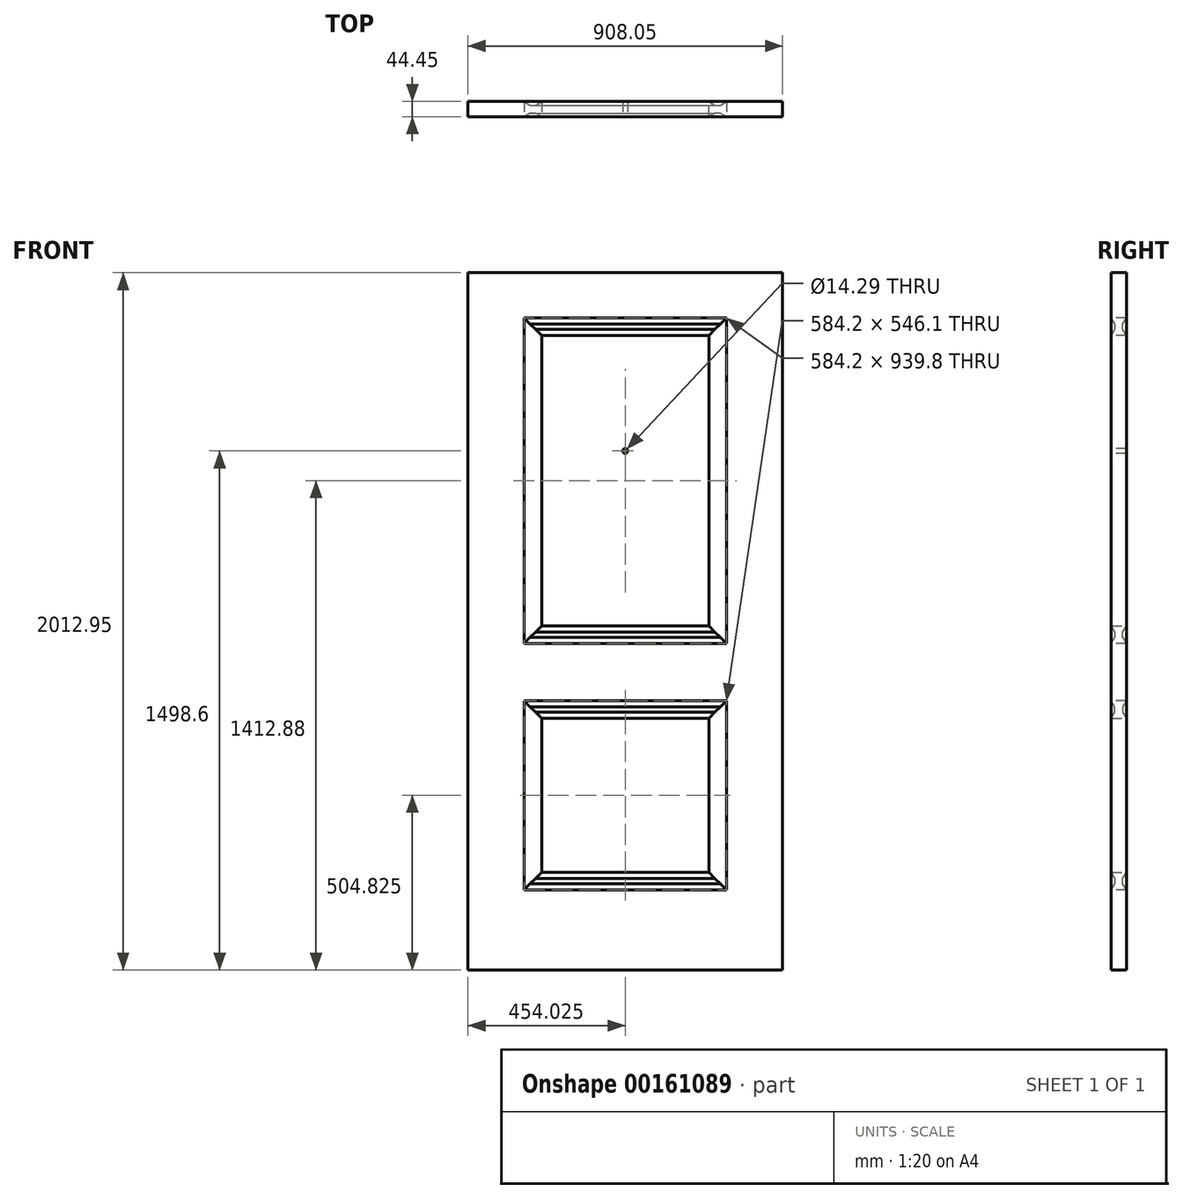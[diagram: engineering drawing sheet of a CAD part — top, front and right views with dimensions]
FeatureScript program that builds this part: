
annotation { "Feature Type Name" : "Feature", "Feature Type Description" : "" }
export const myFeature = defineFeature(function(context is Context, id is Id, definition is map)
    precondition{}
    {
        {
            var Q0;
            Q0=qCreatedBy(makeId("Top.planeOp"),FACE);
            var sketch = newSketch(context, id + "F0", { "sketchPlane" : qUnion([Q0])});
            skLineSegment(sketch, "E0.bottom", {"start": v(0, 0) * mm, "end": v(-908.05, 0) * mm});
            skLineSegment(sketch, "E0.top", {"start": v(0, 44.45) * mm, "end": v(-908.05, 44.45) * mm});
            skLineSegment(sketch, "E0.left", {"start": v(0, 0) * mm, "end": v(0, 44.45) * mm});
            skLineSegment(sketch, "E0.right", {"start": v(-908.05, 0) * mm, "end": v(-908.05, 44.45) * mm});
            skSolve(sketch);
        }
        {
            var Q0;
            Q0=qSketchRegion(id+"F0",true);
            extrude(context, id + "F1", {"entities" : qUnion([Q0]), "depth" : 2012.95 * mm});
        }
        {
            var Q0;
            Q0=qCreatedBy(makeId("Front.planeOp"),FACE);
            var sketch = newSketch(context, id + "F2", { "sketchPlane" : qUnion([Q0])});
            skLineSegment(sketch, "E1.top", {"start": v(-746.12, 942.97) * mm, "end": v(-161.92, 942.98) * mm});
            skLineSegment(sketch, "E1.left", {"start": v(-746.12, 1882.78) * mm, "end": v(-746.12, 942.97) * mm});
            skLineSegment(sketch, "E1.right", {"start": v(-161.93, 1882.78) * mm, "end": v(-161.92, 942.98) * mm});
            skLineSegment(sketch, "E2", {"start": v(-746.12, 1882.78) * mm, "end": v(-454.03, 1882.78) * mm});
            skLineSegment(sketch, "E3", {"start": v(-454.03, 1882.78) * mm, "end": v(-161.93, 1882.78) * mm});
            skPoint(sketch, "E4.0", {"position": v(-454.03, 2012.95) * mm});
            skLineSegment(sketch, "E5.bottom", {"start": v(-746.12, 777.88) * mm, "end": v(-161.92, 777.88) * mm});
            skLineSegment(sketch, "E5.top", {"start": v(-746.12, 231.78) * mm, "end": v(-161.92, 231.78) * mm});
            skLineSegment(sketch, "E5.left", {"start": v(-746.12, 777.88) * mm, "end": v(-746.12, 231.78) * mm});
            skLineSegment(sketch, "E5.right", {"start": v(-161.92, 777.88) * mm, "end": v(-161.92, 231.78) * mm});
            skSolve(sketch);
        }
        {
            var Q0;
            Q0=qSketchRegion(id+"F2",true);
            extrude(context, id + "F3", {"entities" : qUnion([Q0]), "operationType" : NewBodyOperationType.REMOVE, "endBound" : BoundingType.THROUGH_ALL, "oppositeDirection" : true, "depth" : 25.4 * mm});
        }
        {
            var Q0;
            Q0=qCreatedBy(makeId("Top.planeOp"),FACE);
            var sketch = newSketch(context, id + "F4", { "sketchPlane" : qUnion([Q0])});
            skPoint(sketch, "E6.0", {"position": v(-161.93, 22.23) * mm});
            skPoint(sketch, "E7.0", {"position": v(-161.93, 44.45) * mm});
            skLineSegment(sketch, "E8", {"start": v(-161.93, 22.23) * mm, "end": v(-161.93, 44.45) * mm});
            skLineSegment(sketch, "E9", {"start": v(-161.93, 44.45) * mm, "end": v(-179.4, 33.62) * mm});
            skLineSegment(sketch, "E10", {"start": v(-179.4, 33.62) * mm, "end": v(-187.33, 33.62) * mm});
            skLineSegment(sketch, "E11", {"start": v(-187.33, 33.62) * mm, "end": v(-187.33, 59.2) * mm, "construction": true});
            skLineSegment(sketch, "E12", {"start": v(-161.93, 22.23) * mm, "end": v(-138.76, 22.23) * mm, "construction": true});
            skLineSegment(sketch, "E13.MirrorCS", {"start": v(-195.26, 33.62) * mm, "end": v(-187.33, 33.62) * mm});
            skLineSegment(sketch, "E14.MirrorCS", {"start": v(-212.73, 44.45) * mm, "end": v(-195.26, 33.62) * mm});
            skLineSegment(sketch, "E15.MirrorCS", {"start": v(-212.73, 22.23) * mm, "end": v(-212.73, 44.45) * mm});
            skLineSegment(sketch, "E16.MirrorCS", {"start": v(-161.93, 22.23) * mm, "end": v(-161.93, 0) * mm});
            skLineSegment(sketch, "E17.MirrorCS", {"start": v(-161.93, 0) * mm, "end": v(-179.4, 10.83) * mm});
            skLineSegment(sketch, "E18.MirrorCS", {"start": v(-179.4, 10.83) * mm, "end": v(-187.33, 10.83) * mm});
            skLineSegment(sketch, "E19.MirrorCS", {"start": v(-195.26, 10.83) * mm, "end": v(-187.33, 10.83) * mm});
            skLineSegment(sketch, "E20.MirrorCS", {"start": v(-212.73, 0) * mm, "end": v(-195.26, 10.83) * mm});
            skLineSegment(sketch, "E21.MirrorCS", {"start": v(-212.73, 22.23) * mm, "end": v(-212.73, 0) * mm});
            skPoint(sketch, "E22.0", {"position": v(-746.12, 22.23) * mm});
            skLineSegment(sketch, "E23", {"start": v(-746.12, 130.05) * mm, "end": v(-161.92, 130.05) * mm, "construction": true});
            skLineSegment(sketch, "E24", {"start": v(-454.03, 130.05) * mm, "end": v(-454.03, 201.62) * mm, "construction": true});
            skLineSegment(sketch, "E25.MirrorCS", {"start": v(-712.8, 33.62) * mm, "end": v(-720.72, 33.62) * mm});
            skPoint(sketch, "E26.MirrorP", {"position": v(-746.12, 44.45) * mm});
            skLineSegment(sketch, "E27.MirrorCS", {"start": v(-746.12, 0) * mm, "end": v(-728.66, 10.83) * mm});
            skLineSegment(sketch, "E28.MirrorCS", {"start": v(-695.32, 0) * mm, "end": v(-712.8, 10.83) * mm});
            skLineSegment(sketch, "E29.MirrorCS", {"start": v(-746.12, 22.23) * mm, "end": v(-746.12, 0) * mm});
            skLineSegment(sketch, "E30.MirrorCS", {"start": v(-695.32, 22.23) * mm, "end": v(-695.32, 0) * mm});
            skLineSegment(sketch, "E31.MirrorCS", {"start": v(-746.12, 44.45) * mm, "end": v(-728.66, 33.62) * mm});
            skLineSegment(sketch, "E32.MirrorCS", {"start": v(-695.32, 44.45) * mm, "end": v(-712.8, 33.62) * mm});
            skLineSegment(sketch, "E33.MirrorCS", {"start": v(-746.12, 22.23) * mm, "end": v(-746.12, 44.45) * mm});
            skLineSegment(sketch, "E34.MirrorCS", {"start": v(-728.66, 33.62) * mm, "end": v(-720.72, 33.62) * mm});
            skLineSegment(sketch, "E35.MirrorCS", {"start": v(-712.8, 10.83) * mm, "end": v(-720.72, 10.83) * mm});
            skLineSegment(sketch, "E36.MirrorCS", {"start": v(-695.32, 22.23) * mm, "end": v(-695.32, 44.45) * mm});
            skLineSegment(sketch, "E37.MirrorCS", {"start": v(-728.66, 10.83) * mm, "end": v(-720.72, 10.83) * mm});
            skSolve(sketch);
        }
        {
            var Q0;
            Q0=qCreatedBy(makeId("Front.planeOp"),FACE);
            var sketch = newSketch(context, id + "F5", { "sketchPlane" : qUnion([Q0])});
            skPoint(sketch, "E38.0", {"position": v(-746.12, 1882.78) * mm});
            skPoint(sketch, "E39.0", {"position": v(-161.93, 1882.78) * mm});
            skPoint(sketch, "E40.0", {"position": v(-161.92, 942.97) * mm});
            skPoint(sketch, "E41.0", {"position": v(-746.12, 942.97) * mm});
            skPoint(sketch, "E42.0", {"position": v(-746.12, 777.88) * mm});
            skPoint(sketch, "E43.0", {"position": v(-161.92, 777.88) * mm});
            skPoint(sketch, "E44.0", {"position": v(-746.12, 231.78) * mm});
            skPoint(sketch, "E45.0", {"position": v(-161.92, 231.78) * mm});
            skLineSegment(sketch, "E46", {"start": v(-746.12, 1882.78) * mm, "end": v(-454.02, 1590.68) * mm});
            skLineSegment(sketch, "E47", {"start": v(-454.02, 1590.68) * mm, "end": v(-161.92, 1882.78) * mm});
            skLineSegment(sketch, "E48", {"start": v(-746.12, 777.88) * mm, "end": v(-454.02, 485.78) * mm});
            skLineSegment(sketch, "E49", {"start": v(-454.02, 485.78) * mm, "end": v(-161.93, 777.88) * mm});
            skLineSegment(sketch, "E50", {"start": v(-746.12, 1882.78) * mm, "end": v(-876.3, 2012.95) * mm});
            skLineSegment(sketch, "E51", {"start": v(-876.3, 2012.95) * mm, "end": v(-31.75, 2012.95) * mm});
            skLineSegment(sketch, "E52", {"start": v(-31.75, 2012.95) * mm, "end": v(-161.93, 1882.78) * mm});
            skLineSegment(sketch, "E53", {"start": v(-746.12, 777.88) * mm, "end": v(-1981.2, 2012.95) * mm});
            skLineSegment(sketch, "E54", {"start": v(-1981.2, 2012.95) * mm, "end": v(1073.15, 2012.95) * mm});
            skLineSegment(sketch, "E55", {"start": v(1073.15, 2012.95) * mm, "end": v(-161.93, 777.88) * mm});
            skLineSegment(sketch, "E56", {"start": v(-746.12, 942.97) * mm, "end": v(-454.03, 1235.07) * mm});
            skLineSegment(sketch, "E57", {"start": v(-454.02, 1235.08) * mm, "end": v(-161.92, 942.98) * mm});
            skLineSegment(sketch, "E58", {"start": v(-746.12, 231.77) * mm, "end": v(-454.02, 523.88) * mm});
            skLineSegment(sketch, "E59", {"start": v(-454.02, 523.88) * mm, "end": v(-161.92, 231.78) * mm});
            skLineSegment(sketch, "E60", {"start": v(-746.13, 942.97) * mm, "end": v(-1689.1, 0) * mm});
            skLineSegment(sketch, "E61", {"start": v(-1689.1, 0) * mm, "end": v(781.05, 0) * mm});
            skLineSegment(sketch, "E62", {"start": v(781.05, 0) * mm, "end": v(-161.92, 942.97) * mm});
            skLineSegment(sketch, "E63", {"start": v(-161.92, 231.78) * mm, "end": v(69.85, 0) * mm});
            skLineSegment(sketch, "E64", {"start": v(69.85, 0) * mm, "end": v(-977.9, 0) * mm});
            skLineSegment(sketch, "E65", {"start": v(-977.9, 0) * mm, "end": v(-746.12, 231.78) * mm});
            skSolve(sketch);
        }
        {
            var Q0;
            Q0=makeQuery(id+"F3.boolean.opBoolean","COPY",FACE,{"derivedFrom":makeQuery(id+"F3.opExtrude","SWEPT_FACE",FACE,{"disambiguationData":[OSD([sQuery(id+"F2.wireOp",EDGE,"E2"),sQuery(id+"F2.wireOp",EDGE,"E3")])]})});
            var sketch = newSketch(context, id + "F6", { "sketchPlane" : qUnion([Q0])});
            skLineSegment(sketch, "E66.4", {"start": v(-212.73, -44.45) * mm, "end": v(-195.26, -33.62) * mm});
            skLineSegment(sketch, "E66.6", {"start": v(-212.73, -22.23) * mm, "end": v(-212.73, -44.45) * mm});
            skLineSegment(sketch, "E66.8", {"start": v(-212.73, 0) * mm, "end": v(-195.26, -10.83) * mm});
            skLineSegment(sketch, "E66.9", {"start": v(-212.73, -22.23) * mm, "end": v(-212.73, 0) * mm});
            skLineSegment(sketch, "E66.11", {"start": v(-161.93, -44.45) * mm, "end": v(-179.4, -33.62) * mm});
            skLineSegment(sketch, "E66.14", {"start": v(-195.26, -33.62) * mm, "end": v(-187.33, -33.62) * mm});
            skLineSegment(sketch, "E66.16", {"start": v(-161.93, -22.23) * mm, "end": v(-161.93, 0) * mm});
            skLineSegment(sketch, "E66.17", {"start": v(-161.93, 0) * mm, "end": v(-179.4, -10.83) * mm});
            skLineSegment(sketch, "E66.18", {"start": v(-179.4, -10.83) * mm, "end": v(-187.33, -10.83) * mm});
            skLineSegment(sketch, "E66.19", {"start": v(-195.26, -10.83) * mm, "end": v(-187.33, -10.83) * mm});
            skLineSegment(sketch, "E66.25", {"start": v(-161.93, -22.23) * mm, "end": v(-161.93, -44.45) * mm});
            skLineSegment(sketch, "E66.26", {"start": v(-179.4, -33.62) * mm, "end": v(-187.33, -33.62) * mm});
            skLineSegment(sketch, "E67.0", {"start": v(-746.12, -22.23) * mm, "end": v(-746.12, 0) * mm});
            skLineSegment(sketch, "E68.0", {"start": v(-746.12, 0) * mm, "end": v(-728.66, -10.83) * mm});
            skLineSegment(sketch, "E69.0", {"start": v(-728.66, -10.83) * mm, "end": v(-720.72, -10.83) * mm});
            skLineSegment(sketch, "E70.0", {"start": v(-712.8, -10.83) * mm, "end": v(-720.72, -10.83) * mm});
            skLineSegment(sketch, "E71.0", {"start": v(-695.32, 0) * mm, "end": v(-712.8, -10.83) * mm});
            skLineSegment(sketch, "E72.0", {"start": v(-695.32, -22.23) * mm, "end": v(-695.32, 0) * mm});
            skLineSegment(sketch, "E73.0", {"start": v(-695.32, -22.23) * mm, "end": v(-695.32, -44.45) * mm});
            skLineSegment(sketch, "E74.0", {"start": v(-695.32, -44.45) * mm, "end": v(-712.8, -33.62) * mm});
            skLineSegment(sketch, "E75.0", {"start": v(-712.8, -33.62) * mm, "end": v(-720.72, -33.62) * mm});
            skLineSegment(sketch, "E76.0", {"start": v(-728.66, -33.62) * mm, "end": v(-720.72, -33.62) * mm});
            skLineSegment(sketch, "E77.0", {"start": v(-746.12, -44.45) * mm, "end": v(-728.66, -33.62) * mm});
            skLineSegment(sketch, "E78.0", {"start": v(-746.12, -22.23) * mm, "end": v(-746.12, -44.45) * mm});
            skSolve(sketch);
        }
        {
            var Q0;
            Q0=makeQuery(id+"F3.boolean.opBoolean","COPY",FACE,{"derivedFrom":makeQuery(id+"F3.opExtrude","SWEPT_FACE",FACE,{"disambiguationData":[OSD([sQuery(id+"F2.wireOp",EDGE,"E5.top")])]})});
            var sketch = newSketch(context, id + "F7", { "sketchPlane" : qUnion([Q0])});
            skLineSegment(sketch, "E79.0", {"start": v(-212.73, 22.23) * mm, "end": v(-212.73, 0) * mm});
            skLineSegment(sketch, "E79.1", {"start": v(-161.93, 22.23) * mm, "end": v(-161.93, 44.45) * mm});
            skLineSegment(sketch, "E79.2", {"start": v(-161.93, 44.45) * mm, "end": v(-179.4, 33.62) * mm});
            skLineSegment(sketch, "E79.3", {"start": v(-179.4, 33.62) * mm, "end": v(-187.33, 33.62) * mm});
            skLineSegment(sketch, "E79.4", {"start": v(-195.26, 33.62) * mm, "end": v(-187.33, 33.62) * mm});
            skLineSegment(sketch, "E79.5", {"start": v(-212.73, 44.45) * mm, "end": v(-195.26, 33.62) * mm});
            skLineSegment(sketch, "E79.6", {"start": v(-212.73, 22.23) * mm, "end": v(-212.73, 44.45) * mm});
            skLineSegment(sketch, "E79.7", {"start": v(-161.93, 22.23) * mm, "end": v(-161.93, 0) * mm});
            skLineSegment(sketch, "E79.8", {"start": v(-161.93, 0) * mm, "end": v(-179.4, 10.83) * mm});
            skLineSegment(sketch, "E79.9", {"start": v(-179.4, 10.83) * mm, "end": v(-187.33, 10.83) * mm});
            skLineSegment(sketch, "E79.10", {"start": v(-195.26, 10.83) * mm, "end": v(-187.33, 10.83) * mm});
            skLineSegment(sketch, "E79.11", {"start": v(-212.73, 0) * mm, "end": v(-195.26, 10.83) * mm});
            skLineSegment(sketch, "E80.0", {"start": v(-746.12, 44.45) * mm, "end": v(-728.66, 33.62) * mm});
            skLineSegment(sketch, "E81.0", {"start": v(-746.12, 22.23) * mm, "end": v(-746.12, 44.45) * mm});
            skLineSegment(sketch, "E82.0", {"start": v(-746.12, 22.23) * mm, "end": v(-746.12, 0) * mm});
            skLineSegment(sketch, "E83.0", {"start": v(-746.12, 0) * mm, "end": v(-728.66, 10.83) * mm});
            skLineSegment(sketch, "E84.0", {"start": v(-728.66, 10.83) * mm, "end": v(-720.72, 10.83) * mm});
            skLineSegment(sketch, "E85.0", {"start": v(-712.8, 10.83) * mm, "end": v(-720.72, 10.83) * mm});
            skLineSegment(sketch, "E86.0", {"start": v(-695.32, 0) * mm, "end": v(-712.8, 10.83) * mm});
            skLineSegment(sketch, "E87.0", {"start": v(-695.32, 22.23) * mm, "end": v(-695.32, 0) * mm});
            skLineSegment(sketch, "E88.0", {"start": v(-695.32, 22.23) * mm, "end": v(-695.32, 44.45) * mm});
            skLineSegment(sketch, "E89.0", {"start": v(-695.32, 44.45) * mm, "end": v(-712.8, 33.62) * mm});
            skLineSegment(sketch, "E90.0", {"start": v(-712.8, 33.62) * mm, "end": v(-720.72, 33.62) * mm});
            skPoint(sketch, "E91.0", {"position": v(-724.7, 33.62) * mm});
            skLineSegment(sketch, "E92.0", {"start": v(-728.66, 33.62) * mm, "end": v(-720.72, 33.62) * mm});
            skSolve(sketch);
        }
        {
            var Q0;
            Q0=qSketchRegion(id+"F6",true);
            var Q1;
            Q1=makeQuery(id+"F3.boolean.opBoolean","COPY",FACE,{"derivedFrom":makeQuery(id+"F3.opExtrude","SWEPT_FACE",FACE,{"disambiguationData":[OSD([sQuery(id+"F2.wireOp",EDGE,"E1.top")])]})});
            extrude(context, id + "F8", {"entities" : qUnion([Q0]), "operationType" : NewBodyOperationType.ADD, "endBound" : BoundingType.UP_TO_SURFACE, "endBoundEntityFace" : qUnion([Q1]), "depth" : 307.34 * mm});
        }
        {
            var Q0;
            Q0=qSketchRegion(id+"F7",true);
            var Q1;
            Q1=makeQuery(id+"F3.boolean.opBoolean","COPY",FACE,{"derivedFrom":makeQuery(id+"F3.opExtrude","SWEPT_FACE",FACE,{"disambiguationData":[OSD([sQuery(id+"F2.wireOp",EDGE,"E5.bottom")])]})});
            extrude(context, id + "F9", {"entities" : qUnion([Q0]), "operationType" : NewBodyOperationType.ADD, "endBound" : BoundingType.UP_TO_SURFACE, "endBoundEntityFace" : qUnion([Q1]), "depth" : 25.4 * mm});
        }
        {
            var Q0;
            Q0=qCreatedBy(makeId("Front.planeOp"),FACE);
            var sketch = newSketch(context, id + "F10", { "sketchPlane" : qUnion([Q0])});
            skLineSegment(sketch, "E93.0", {"start": v(-454.02, 1590.68) * mm, "end": v(-161.92, 1882.78) * mm});
            skLineSegment(sketch, "E94.0", {"start": v(-746.12, 1882.78) * mm, "end": v(-454.02, 1590.68) * mm});
            skLineSegment(sketch, "E95.0", {"start": v(-454.02, 1235.08) * mm, "end": v(-161.92, 942.98) * mm});
            skLineSegment(sketch, "E96.0", {"start": v(-746.12, 942.97) * mm, "end": v(-454.03, 1235.07) * mm});
            skLineSegment(sketch, "E97.0", {"start": v(-454.02, 485.78) * mm, "end": v(-161.92, 777.88) * mm});
            skLineSegment(sketch, "E98.0", {"start": v(-746.12, 777.88) * mm, "end": v(-454.02, 485.78) * mm});
            skLineSegment(sketch, "E99.0", {"start": v(-746.12, 231.77) * mm, "end": v(-454.02, 523.88) * mm});
            skLineSegment(sketch, "E100.0", {"start": v(-454.02, 523.88) * mm, "end": v(-161.92, 231.78) * mm});
            skLineSegment(sketch, "E101", {"start": v(-746.12, 1882.78) * mm, "end": v(-161.92, 1882.78) * mm});
            skLineSegment(sketch, "E102", {"start": v(-746.12, 942.97) * mm, "end": v(-161.92, 942.97) * mm});
            skLineSegment(sketch, "E103", {"start": v(-161.92, 777.88) * mm, "end": v(-746.12, 777.88) * mm});
            skLineSegment(sketch, "E104", {"start": v(-746.12, 231.77) * mm, "end": v(-161.92, 231.78) * mm});
            skSolve(sketch);
        }
        {
            var Q0;
            Q0=qSketchRegion(id+"F10",true);
            extrude(context, id + "F11", {"entities" : qUnion([Q0]), "operationType" : NewBodyOperationType.REMOVE, "endBound" : BoundingType.THROUGH_ALL, "oppositeDirection" : true, "depth" : 25.4 * mm});
        }
        {
            var Q0;
            Q0=qCreatedBy(makeId("Right.planeOp"),FACE);
            var sketch = newSketch(context, id + "F12", { "sketchPlane" : qUnion([Q0])});
            skLineSegment(sketch, "E105.0.0", {"start": v(0, 1882.78) * mm, "end": v(44.45, 1882.78) * mm});
            skLineSegment(sketch, "E105.0.1", {"start": v(44.45, 1882.78) * mm, "end": v(33.62, 1865.3) * mm});
            skLineSegment(sketch, "E105.0.2", {"start": v(33.62, 1865.3) * mm, "end": v(33.62, 1849.44) * mm});
            skLineSegment(sketch, "E105.0.3", {"start": v(33.62, 1849.44) * mm, "end": v(44.45, 1831.98) * mm});
            skLineSegment(sketch, "E105.0.4", {"start": v(44.45, 1831.97) * mm, "end": v(0, 1831.97) * mm});
            skLineSegment(sketch, "E105.0.5", {"start": v(0, 1831.98) * mm, "end": v(10.83, 1849.44) * mm});
            skLineSegment(sketch, "E105.0.6", {"start": v(10.83, 1849.44) * mm, "end": v(10.83, 1865.3) * mm});
            skLineSegment(sketch, "E105.0.7", {"start": v(10.83, 1865.3) * mm, "end": v(0, 1882.77) * mm});
            skLineSegment(sketch, "E106.0.0", {"start": v(0, 942.98) * mm, "end": v(10.83, 960.44) * mm});
            skLineSegment(sketch, "E106.0.1", {"start": v(10.83, 960.44) * mm, "end": v(10.83, 976.3) * mm});
            skLineSegment(sketch, "E106.0.2", {"start": v(10.83, 976.3) * mm, "end": v(0, 993.77) * mm});
            skLineSegment(sketch, "E106.0.3", {"start": v(0, 993.77) * mm, "end": v(44.45, 993.77) * mm});
            skLineSegment(sketch, "E106.0.4", {"start": v(44.45, 993.77) * mm, "end": v(33.62, 976.3) * mm});
            skLineSegment(sketch, "E106.0.5", {"start": v(33.62, 976.3) * mm, "end": v(33.62, 960.44) * mm});
            skLineSegment(sketch, "E106.0.6", {"start": v(33.62, 960.44) * mm, "end": v(44.45, 942.97) * mm});
            skLineSegment(sketch, "E106.0.7", {"start": v(44.45, 942.98) * mm, "end": v(0, 942.98) * mm});
            skLineSegment(sketch, "E107.0.0", {"start": v(33.62, 760.4) * mm, "end": v(33.62, 744.54) * mm});
            skLineSegment(sketch, "E107.0.1", {"start": v(33.62, 744.54) * mm, "end": v(44.45, 727.07) * mm});
            skLineSegment(sketch, "E107.0.2", {"start": v(44.45, 727.07) * mm, "end": v(0, 727.07) * mm});
            skLineSegment(sketch, "E107.0.3", {"start": v(0, 727.08) * mm, "end": v(10.83, 744.54) * mm});
            skLineSegment(sketch, "E107.0.4", {"start": v(10.83, 744.54) * mm, "end": v(10.83, 760.4) * mm});
            skLineSegment(sketch, "E107.0.5", {"start": v(10.83, 760.4) * mm, "end": v(0, 777.88) * mm});
            skLineSegment(sketch, "E107.0.6", {"start": v(0, 777.88) * mm, "end": v(44.45, 777.88) * mm});
            skLineSegment(sketch, "E107.0.7", {"start": v(44.45, 777.87) * mm, "end": v(33.62, 760.4) * mm});
            skLineSegment(sketch, "E108.0.0", {"start": v(33.62, 249.24) * mm, "end": v(44.45, 231.77) * mm});
            skLineSegment(sketch, "E108.0.1", {"start": v(44.45, 231.78) * mm, "end": v(0, 231.78) * mm});
            skLineSegment(sketch, "E108.0.2", {"start": v(0, 231.78) * mm, "end": v(10.83, 249.24) * mm});
            skLineSegment(sketch, "E108.0.3", {"start": v(10.83, 249.24) * mm, "end": v(10.83, 265.1) * mm});
            skLineSegment(sketch, "E108.0.4", {"start": v(10.83, 265.1) * mm, "end": v(0, 282.58) * mm});
            skLineSegment(sketch, "E108.0.5", {"start": v(0, 282.58) * mm, "end": v(44.45, 282.58) * mm});
            skLineSegment(sketch, "E108.0.6", {"start": v(44.45, 282.57) * mm, "end": v(33.62, 265.1) * mm});
            skLineSegment(sketch, "E108.0.7", {"start": v(33.62, 265.1) * mm, "end": v(33.62, 249.24) * mm});
            skSolve(sketch);
        }
        {
            var Q0;
            Q0=qSketchRegion(id+"F12",true);
            var Q1;
            Q1=makeQuery(id+"F1.opExtrude","SWEPT_FACE",FACE,{"disambiguationData":[OSD([sQuery(id+"F0.wireOp",EDGE,"E0.right")])]});
            extrude(context, id + "F13", {"entities" : qUnion([Q0]), "endBound" : BoundingType.UP_TO_SURFACE, "oppositeDirection" : true, "endBoundEntityFace" : qUnion([Q1]), "depth" : 25.4 * mm});
        }
        {
            var Q0;
            Q0=qCreatedBy(makeId("Front.planeOp"),FACE);
            var sketch = newSketch(context, id + "F14", { "sketchPlane" : qUnion([Q0])});
            skLineSegment(sketch, "E109.0", {"start": v(-746.12, 231.77) * mm, "end": v(-454.02, 523.88) * mm});
            skLineSegment(sketch, "E110.0", {"start": v(-746.12, 777.88) * mm, "end": v(-454.02, 485.78) * mm});
            skLineSegment(sketch, "E111.0", {"start": v(-454.02, 523.88) * mm, "end": v(-161.92, 231.78) * mm});
            skLineSegment(sketch, "E112.0", {"start": v(-454.02, 485.78) * mm, "end": v(-161.92, 777.88) * mm});
            skLineSegment(sketch, "E113", {"start": v(-161.92, 777.88) * mm, "end": v(-161.92, 231.78) * mm});
            skLineSegment(sketch, "E114", {"start": v(-746.12, 777.88) * mm, "end": v(-746.12, 231.77) * mm});
            skLineSegment(sketch, "E115.0", {"start": v(-454.02, 1590.68) * mm, "end": v(-161.92, 1882.78) * mm});
            skLineSegment(sketch, "E116.0", {"start": v(-746.12, 1882.78) * mm, "end": v(-454.02, 1590.68) * mm});
            skLineSegment(sketch, "E117.0", {"start": v(-746.12, 942.97) * mm, "end": v(-454.03, 1235.07) * mm});
            skLineSegment(sketch, "E118.0", {"start": v(-454.02, 1235.08) * mm, "end": v(-161.92, 942.98) * mm});
            skLineSegment(sketch, "E119", {"start": v(-161.92, 1882.78) * mm, "end": v(-161.92, 942.98) * mm});
            skLineSegment(sketch, "E120", {"start": v(-746.12, 942.97) * mm, "end": v(-746.12, 1882.78) * mm});
            skSolve(sketch);
        }
        {
            var Q0;
            Q0=qSketchRegion(id+"F14",true);
            extrude(context, id + "F15", {"entities" : qUnion([Q0]), "operationType" : NewBodyOperationType.REMOVE, "endBound" : BoundingType.THROUGH_ALL, "oppositeDirection" : true, "depth" : 25.4 * mm});
        }
        {
            var Q0;
            Q0=makeQuery(id+"F1.opExtrude","SWEPT_BODY",BODY,{"disambiguationData":[OSD([sQuery(id+"F0.wireOp",EDGE,"E0.bottom"),sQuery(id+"F0.wireOp",EDGE,"E0.top"),sQuery(id+"F0.wireOp",EDGE,"E0.left"),sQuery(id+"F0.wireOp",EDGE,"E0.right")])]});
            var Q1;
            Q1=makeQuery(id+"F15.boolean.opBoolean","SPLIT",BODY,{"disambiguationData":[OD(0.0)],"derivedFrom":makeQuery(id+"F13.opExtrude","SWEPT_BODY",BODY,{"disambiguationData":[OSD([sQuery(id+"F12.wireOp",EDGE,"E105.0.0"),sQuery(id+"F12.wireOp",EDGE,"E105.0.1"),sQuery(id+"F12.wireOp",EDGE,"E105.0.2"),sQuery(id+"F12.wireOp",EDGE,"E105.0.3"),sQuery(id+"F12.wireOp",EDGE,"E105.0.4"),sQuery(id+"F12.wireOp",EDGE,"E105.0.5"),sQuery(id+"F12.wireOp",EDGE,"E105.0.6"),sQuery(id+"F12.wireOp",EDGE,"E105.0.7")])]})});
            var Q2;
            Q2=makeQuery(id+"F15.boolean.opBoolean","SPLIT",BODY,{"disambiguationData":[OD(1.0)],"derivedFrom":makeQuery(id+"F13.opExtrude","SWEPT_BODY",BODY,{"disambiguationData":[OSD([sQuery(id+"F12.wireOp",EDGE,"E105.0.0"),sQuery(id+"F12.wireOp",EDGE,"E105.0.1"),sQuery(id+"F12.wireOp",EDGE,"E105.0.2"),sQuery(id+"F12.wireOp",EDGE,"E105.0.3"),sQuery(id+"F12.wireOp",EDGE,"E105.0.4"),sQuery(id+"F12.wireOp",EDGE,"E105.0.5"),sQuery(id+"F12.wireOp",EDGE,"E105.0.6"),sQuery(id+"F12.wireOp",EDGE,"E105.0.7")])]})});
            var Q3;
            Q3=makeQuery(id+"F15.boolean.opBoolean","SPLIT",BODY,{"disambiguationData":[OD(2.0)],"derivedFrom":makeQuery(id+"F13.opExtrude","SWEPT_BODY",BODY,{"disambiguationData":[OSD([sQuery(id+"F12.wireOp",EDGE,"E105.0.0"),sQuery(id+"F12.wireOp",EDGE,"E105.0.1"),sQuery(id+"F12.wireOp",EDGE,"E105.0.2"),sQuery(id+"F12.wireOp",EDGE,"E105.0.3"),sQuery(id+"F12.wireOp",EDGE,"E105.0.4"),sQuery(id+"F12.wireOp",EDGE,"E105.0.5"),sQuery(id+"F12.wireOp",EDGE,"E105.0.6"),sQuery(id+"F12.wireOp",EDGE,"E105.0.7")])]})});
            var Q4;
            Q4=makeQuery(id+"F15.boolean.opBoolean","SPLIT",BODY,{"disambiguationData":[OD(0.0)],"derivedFrom":makeQuery(id+"F13.opExtrude","SWEPT_BODY",BODY,{"disambiguationData":[OSD([sQuery(id+"F12.wireOp",EDGE,"E106.0.0"),sQuery(id+"F12.wireOp",EDGE,"E106.0.1"),sQuery(id+"F12.wireOp",EDGE,"E106.0.2"),sQuery(id+"F12.wireOp",EDGE,"E106.0.3"),sQuery(id+"F12.wireOp",EDGE,"E106.0.4"),sQuery(id+"F12.wireOp",EDGE,"E106.0.5"),sQuery(id+"F12.wireOp",EDGE,"E106.0.6"),sQuery(id+"F12.wireOp",EDGE,"E106.0.7")])]})});
            var Q5;
            Q5=makeQuery(id+"F15.boolean.opBoolean","SPLIT",BODY,{"disambiguationData":[OD(1.0)],"derivedFrom":makeQuery(id+"F13.opExtrude","SWEPT_BODY",BODY,{"disambiguationData":[OSD([sQuery(id+"F12.wireOp",EDGE,"E106.0.0"),sQuery(id+"F12.wireOp",EDGE,"E106.0.1"),sQuery(id+"F12.wireOp",EDGE,"E106.0.2"),sQuery(id+"F12.wireOp",EDGE,"E106.0.3"),sQuery(id+"F12.wireOp",EDGE,"E106.0.4"),sQuery(id+"F12.wireOp",EDGE,"E106.0.5"),sQuery(id+"F12.wireOp",EDGE,"E106.0.6"),sQuery(id+"F12.wireOp",EDGE,"E106.0.7")])]})});
            var Q6;
            Q6=makeQuery(id+"F15.boolean.opBoolean","SPLIT",BODY,{"disambiguationData":[OD(2.0)],"derivedFrom":makeQuery(id+"F13.opExtrude","SWEPT_BODY",BODY,{"disambiguationData":[OSD([sQuery(id+"F12.wireOp",EDGE,"E106.0.0"),sQuery(id+"F12.wireOp",EDGE,"E106.0.1"),sQuery(id+"F12.wireOp",EDGE,"E106.0.2"),sQuery(id+"F12.wireOp",EDGE,"E106.0.3"),sQuery(id+"F12.wireOp",EDGE,"E106.0.4"),sQuery(id+"F12.wireOp",EDGE,"E106.0.5"),sQuery(id+"F12.wireOp",EDGE,"E106.0.6"),sQuery(id+"F12.wireOp",EDGE,"E106.0.7")])]})});
            var Q7;
            Q7=makeQuery(id+"F15.boolean.opBoolean","SPLIT",BODY,{"disambiguationData":[OD(0.0)],"derivedFrom":makeQuery(id+"F13.opExtrude","SWEPT_BODY",BODY,{"disambiguationData":[OSD([sQuery(id+"F12.wireOp",EDGE,"E107.0.0"),sQuery(id+"F12.wireOp",EDGE,"E107.0.1"),sQuery(id+"F12.wireOp",EDGE,"E107.0.2"),sQuery(id+"F12.wireOp",EDGE,"E107.0.3"),sQuery(id+"F12.wireOp",EDGE,"E107.0.4"),sQuery(id+"F12.wireOp",EDGE,"E107.0.5"),sQuery(id+"F12.wireOp",EDGE,"E107.0.6"),sQuery(id+"F12.wireOp",EDGE,"E107.0.7")])]})});
            var Q8;
            Q8=makeQuery(id+"F15.boolean.opBoolean","SPLIT",BODY,{"disambiguationData":[OD(1.0)],"derivedFrom":makeQuery(id+"F13.opExtrude","SWEPT_BODY",BODY,{"disambiguationData":[OSD([sQuery(id+"F12.wireOp",EDGE,"E107.0.0"),sQuery(id+"F12.wireOp",EDGE,"E107.0.1"),sQuery(id+"F12.wireOp",EDGE,"E107.0.2"),sQuery(id+"F12.wireOp",EDGE,"E107.0.3"),sQuery(id+"F12.wireOp",EDGE,"E107.0.4"),sQuery(id+"F12.wireOp",EDGE,"E107.0.5"),sQuery(id+"F12.wireOp",EDGE,"E107.0.6"),sQuery(id+"F12.wireOp",EDGE,"E107.0.7")])]})});
            var Q9;
            Q9=makeQuery(id+"F15.boolean.opBoolean","SPLIT",BODY,{"disambiguationData":[OD(2.0)],"derivedFrom":makeQuery(id+"F13.opExtrude","SWEPT_BODY",BODY,{"disambiguationData":[OSD([sQuery(id+"F12.wireOp",EDGE,"E107.0.0"),sQuery(id+"F12.wireOp",EDGE,"E107.0.1"),sQuery(id+"F12.wireOp",EDGE,"E107.0.2"),sQuery(id+"F12.wireOp",EDGE,"E107.0.3"),sQuery(id+"F12.wireOp",EDGE,"E107.0.4"),sQuery(id+"F12.wireOp",EDGE,"E107.0.5"),sQuery(id+"F12.wireOp",EDGE,"E107.0.6"),sQuery(id+"F12.wireOp",EDGE,"E107.0.7")])]})});
            var Q10;
            Q10=makeQuery(id+"F15.boolean.opBoolean","SPLIT",BODY,{"disambiguationData":[OD(0.0)],"derivedFrom":makeQuery(id+"F13.opExtrude","SWEPT_BODY",BODY,{"disambiguationData":[OSD([sQuery(id+"F12.wireOp",EDGE,"E108.0.0"),sQuery(id+"F12.wireOp",EDGE,"E108.0.1"),sQuery(id+"F12.wireOp",EDGE,"E108.0.2"),sQuery(id+"F12.wireOp",EDGE,"E108.0.3"),sQuery(id+"F12.wireOp",EDGE,"E108.0.4"),sQuery(id+"F12.wireOp",EDGE,"E108.0.5"),sQuery(id+"F12.wireOp",EDGE,"E108.0.6"),sQuery(id+"F12.wireOp",EDGE,"E108.0.7")])]})});
            var Q11;
            Q11=makeQuery(id+"F15.boolean.opBoolean","SPLIT",BODY,{"disambiguationData":[OD(1.0)],"derivedFrom":makeQuery(id+"F13.opExtrude","SWEPT_BODY",BODY,{"disambiguationData":[OSD([sQuery(id+"F12.wireOp",EDGE,"E108.0.0"),sQuery(id+"F12.wireOp",EDGE,"E108.0.1"),sQuery(id+"F12.wireOp",EDGE,"E108.0.2"),sQuery(id+"F12.wireOp",EDGE,"E108.0.3"),sQuery(id+"F12.wireOp",EDGE,"E108.0.4"),sQuery(id+"F12.wireOp",EDGE,"E108.0.5"),sQuery(id+"F12.wireOp",EDGE,"E108.0.6"),sQuery(id+"F12.wireOp",EDGE,"E108.0.7")])]})});
            var Q12;
            Q12=makeQuery(id+"F15.boolean.opBoolean","SPLIT",BODY,{"disambiguationData":[OD(2.0)],"derivedFrom":makeQuery(id+"F13.opExtrude","SWEPT_BODY",BODY,{"disambiguationData":[OSD([sQuery(id+"F12.wireOp",EDGE,"E108.0.0"),sQuery(id+"F12.wireOp",EDGE,"E108.0.1"),sQuery(id+"F12.wireOp",EDGE,"E108.0.2"),sQuery(id+"F12.wireOp",EDGE,"E108.0.3"),sQuery(id+"F12.wireOp",EDGE,"E108.0.4"),sQuery(id+"F12.wireOp",EDGE,"E108.0.5"),sQuery(id+"F12.wireOp",EDGE,"E108.0.6"),sQuery(id+"F12.wireOp",EDGE,"E108.0.7")])]})});
            booleanBodies(context, id + "F16", {"operationType" : BooleanOperationType.UNION, "tools" : qUnion([Q0, Q1, Q2, Q3, Q4, Q5, Q6, Q7, Q8, Q9, Q10, Q11, Q12])});
        }
        {
            var Q0;
            Q0=makeQuery(id+"F15.boolean.opBoolean","SPLIT",FACE,{"disambiguationData":[TD([makeQuery(id+"F15.opExtrude","SWEPT_FACE",FACE,{"disambiguationData":[OSD([sQuery(id+"F14.wireOp",EDGE,"E117.0")])]})])],"derivedFrom":makeQuery(id+"F13.opExtrude","SWEPT_FACE",FACE,{"disambiguationData":[OSD([sQuery(id+"F12.wireOp",EDGE,"E106.0.3")])]})});
            var sketch = newSketch(context, id + "F17", { "sketchPlane" : qUnion([Q0])});
            skLineSegment(sketch, "E121.0.0", {"start": v(-212.73, 44.45) * mm, "end": v(-695.33, 44.45) * mm});
            skLineSegment(sketch, "E121.0.1", {"start": v(-695.32, 44.45) * mm, "end": v(-695.32, 0) * mm});
            skLineSegment(sketch, "E121.0.2", {"start": v(-695.33, 0) * mm, "end": v(-212.73, 0) * mm});
            skLineSegment(sketch, "E121.0.3", {"start": v(-212.73, 0) * mm, "end": v(-212.73, 44.45) * mm});
            skSolve(sketch);
        }
        {
            var Q0;
            Q0=qSketchRegion(id+"F17",true);
            var Q1;
            Q1=makeQuery(id+"F15.boolean.opBoolean","SPLIT",FACE,{"disambiguationData":[TD([makeQuery(id+"F15.opExtrude","SWEPT_FACE",FACE,{"disambiguationData":[OSD([sQuery(id+"F14.wireOp",EDGE,"E115.0")])]})])],"derivedFrom":makeQuery(id+"F13.opExtrude","SWEPT_FACE",FACE,{"disambiguationData":[OSD([sQuery(id+"F12.wireOp",EDGE,"E105.0.4")])]})});
            extrude(context, id + "F18", {"entities" : qUnion([Q0]), "operationType" : NewBodyOperationType.ADD, "endBound" : BoundingType.UP_TO_SURFACE, "endBoundEntityFace" : qUnion([Q1]), "depth" : 25.4 * mm});
        }
        {
            var Q0;
            {var subQ0=sQuery(id+"F14.wireOp",EDGE,"E109.0");Q0=makeQuery(id+"F15.boolean.opBoolean","SPLIT",FACE,{"disambiguationData":[TD([makeQuery(id+"F15.opExtrude","SWEPT_FACE",FACE,{"disambiguationData":[OSD([subQ0]),TDD([makeQuery(id+"F14.imprint","IMPRINT",EDGE,{"disambiguationData":[TD([[makeQuery(id+"F14.imprint","INTERSECT",VERTEX,{"derivedFrom":[subQ0,sQuery(id+"F14.wireOp",EDGE,"E114")]}),-1.0]])],"derivedFrom":subQ0})])]})])],"derivedFrom":makeQuery(id+"F13.opExtrude","SWEPT_FACE",FACE,{"disambiguationData":[OSD([sQuery(id+"F12.wireOp",EDGE,"E108.0.5")])]})});}
            var sketch = newSketch(context, id + "F19", { "sketchPlane" : qUnion([Q0])});
            skLineSegment(sketch, "E122.0.0", {"start": v(-695.33, 0) * mm, "end": v(-212.73, 0) * mm});
            skLineSegment(sketch, "E122.0.1", {"start": v(-212.73, 0) * mm, "end": v(-212.73, 44.45) * mm});
            skLineSegment(sketch, "E122.0.2", {"start": v(-212.73, 44.45) * mm, "end": v(-695.33, 44.45) * mm});
            skLineSegment(sketch, "E122.0.3", {"start": v(-695.32, 44.45) * mm, "end": v(-695.32, 0) * mm});
            skSolve(sketch);
        }
        {
            var Q0;
            Q0=qSketchRegion(id+"F19",true);
            var Q1;
            {var subQ0=sQuery(id+"F14.wireOp",EDGE,"E110.0");Q1=makeQuery(id+"F15.boolean.opBoolean","SPLIT",FACE,{"disambiguationData":[TD([makeQuery(id+"F15.opExtrude","SWEPT_FACE",FACE,{"disambiguationData":[OSD([subQ0]),TDD([makeQuery(id+"F14.imprint","IMPRINT",EDGE,{"disambiguationData":[TD([[makeQuery(id+"F14.imprint","INTERSECT",VERTEX,{"derivedFrom":[subQ0,sQuery(id+"F14.wireOp",EDGE,"E114")]}),-1.0]])],"derivedFrom":subQ0})])]})])],"derivedFrom":makeQuery(id+"F13.opExtrude","SWEPT_FACE",FACE,{"disambiguationData":[OSD([sQuery(id+"F12.wireOp",EDGE,"E107.0.2")])]})});}
            extrude(context, id + "F20", {"entities" : qUnion([Q0]), "operationType" : NewBodyOperationType.ADD, "endBound" : BoundingType.UP_TO_SURFACE, "endBoundEntityFace" : qUnion([Q1]), "depth" : 25.4 * mm});
        }
        {
            var Q0;
            Q0=qCreatedBy(makeId("Front.planeOp"),FACE);
            var sketch = newSketch(context, id + "F21", { "sketchPlane" : qUnion([Q0])});
            skLineSegment(sketch, "E123.0", {"start": v(0, 0) * mm, "end": v(-908.05, 0) * mm, "construction": true});
            skLineSegment(sketch, "E124", {"start": v(-454.03, 0) * mm, "end": v(-454.03, 1498.6) * mm, "construction": true});
            skCircle(sketch, "E125", {"center": v(-454.03, 1498.6) * mm, "radius": 7.14 * mm});
            skSolve(sketch);
        }
        {
            var Q0;
            Q0 = qSketchRegion(id + "F21", true);
            extrude(context, id + "F22", {"entities" : qUnion([Q0]), "operationType" : NewBodyOperationType.REMOVE, "endBound" : BoundingType.THROUGH_ALL, "oppositeDirection" : true, "depth" : 185.42 * mm});
        }
    });
